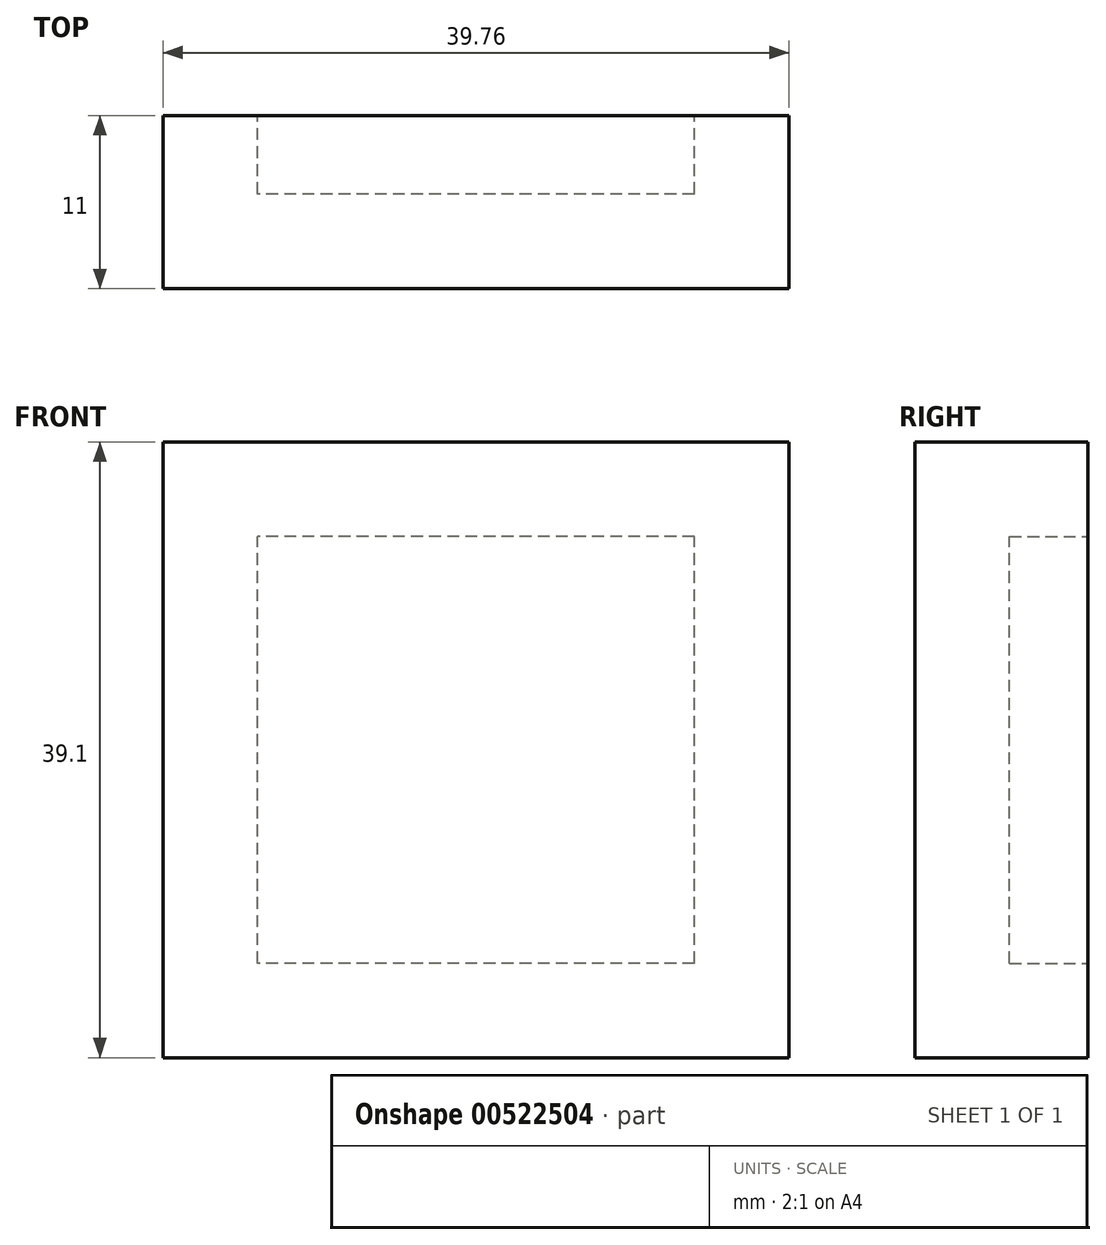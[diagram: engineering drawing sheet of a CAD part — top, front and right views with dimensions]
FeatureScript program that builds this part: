
annotation { "Feature Type Name" : "Feature", "Feature Type Description" : "" }
export const myFeature = defineFeature(function(context is Context, id is Id, definition is map)
    precondition{}
    {
        {
            var Q0;
            Q0=qCreatedBy(makeId("Front.planeOp"),FACE);
            var sketch = newSketch(context, id + "F0", { "sketchPlane" : qUnion([Q0])});
            skLineSegment(sketch, "E0.bottom", {"start": v(13.88, -13.55) * mm, "end": v(-13.88, -13.55) * mm});
            skLineSegment(sketch, "E0.top", {"start": v(13.88, 13.55) * mm, "end": v(-13.88, 13.55) * mm});
            skLineSegment(sketch, "E0.left", {"start": v(13.88, -13.55) * mm, "end": v(13.88, 13.55) * mm});
            skLineSegment(sketch, "E0.right", {"start": v(-13.88, -13.55) * mm, "end": v(-13.88, 13.55) * mm});
            skPoint(sketch, "E0.middle", {"position": v(0, 0) * mm});
            skSolve(sketch);
        }
        {
            var Q0;
            Q0 = qSketchRegion(id + "F0", true);
            extrude(context, id + "F1", {"entities" : qUnion([Q0]), "depth" : 5 * mm, "offsetDistance" : 25.4 * mm});
        }
        {
            var Q0;
            Q0=makeQuery(id+"F1.opExtrude","CAP_FACE",FACE,{"disambiguationData":[OSD([sQuery(id+"F0.wireOp",EDGE,"E0.bottom"),sQuery(id+"F0.wireOp",EDGE,"E0.top"),sQuery(id+"F0.wireOp",EDGE,"E0.left"),sQuery(id+"F0.wireOp",EDGE,"E0.right")])],"isStart":false});
            shell(context, id + "F2", {"entities" : qUnion([Q0]), "thickness" : 5 * mm});
        }
        {
            var Q0;
            Q0=makeQuery(id+"F1.opExtrude","CAP_FACE",FACE,{"disambiguationData":[OSD([sQuery(id+"F0.wireOp",EDGE,"E0.bottom"),sQuery(id+"F0.wireOp",EDGE,"E0.top"),sQuery(id+"F0.wireOp",EDGE,"E0.left"),sQuery(id+"F0.wireOp",EDGE,"E0.right")])],"isStart":true});
            shell(context, id + "F3", {"entities" : qUnion([Q0]), "thickness" : 6 * mm, "oppositeDirection" : true});
        }
    });
